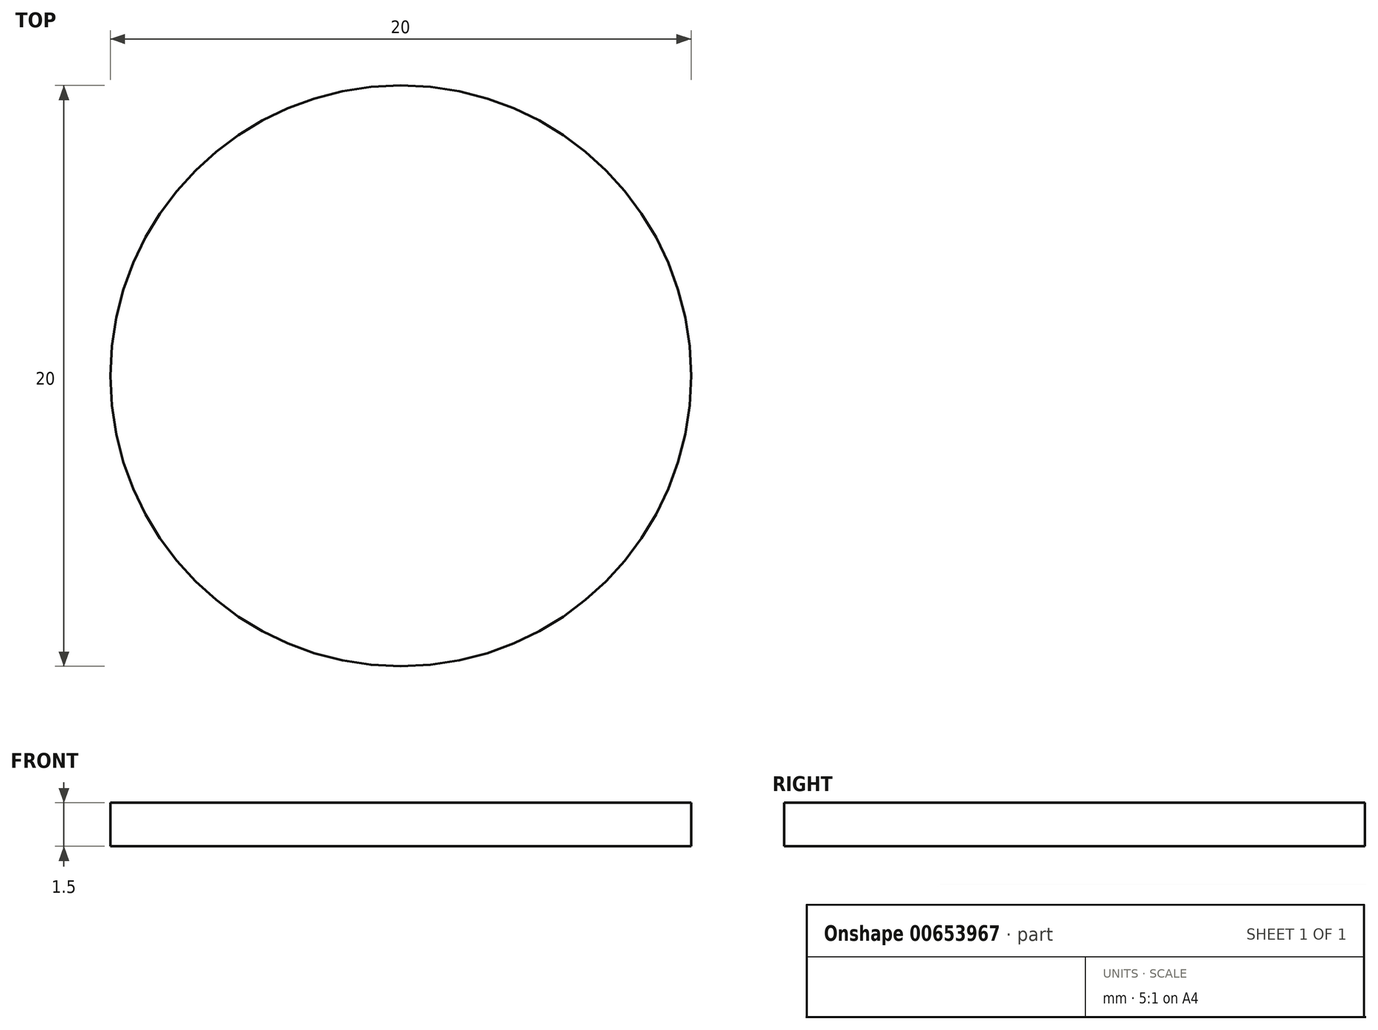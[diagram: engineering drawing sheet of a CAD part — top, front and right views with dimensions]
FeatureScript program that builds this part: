
annotation { "Feature Type Name" : "Feature", "Feature Type Description" : "" }
export const myFeature = defineFeature(function(context is Context, id is Id, definition is map)
    precondition{}
    {
        {
            var Q0;
            Q0=qCreatedBy(makeId("Top.planeOp"),FACE);
            var sketch = newSketch(context, id + "F0", { "sketchPlane" : qUnion([Q0])});
            skCircle(sketch, "E0", {"center": v(0, 0) * mm, "radius": 10 * mm});
            skSolve(sketch);
        }
        {
            var Q0;
            Q0 = qSketchRegion(id + "F0", true);
            extrude(context, id + "F1", {"entities" : qUnion([Q0]), "depth" : 1.5 * mm, "offsetDistance" : 25 * mm});
        }
    });
